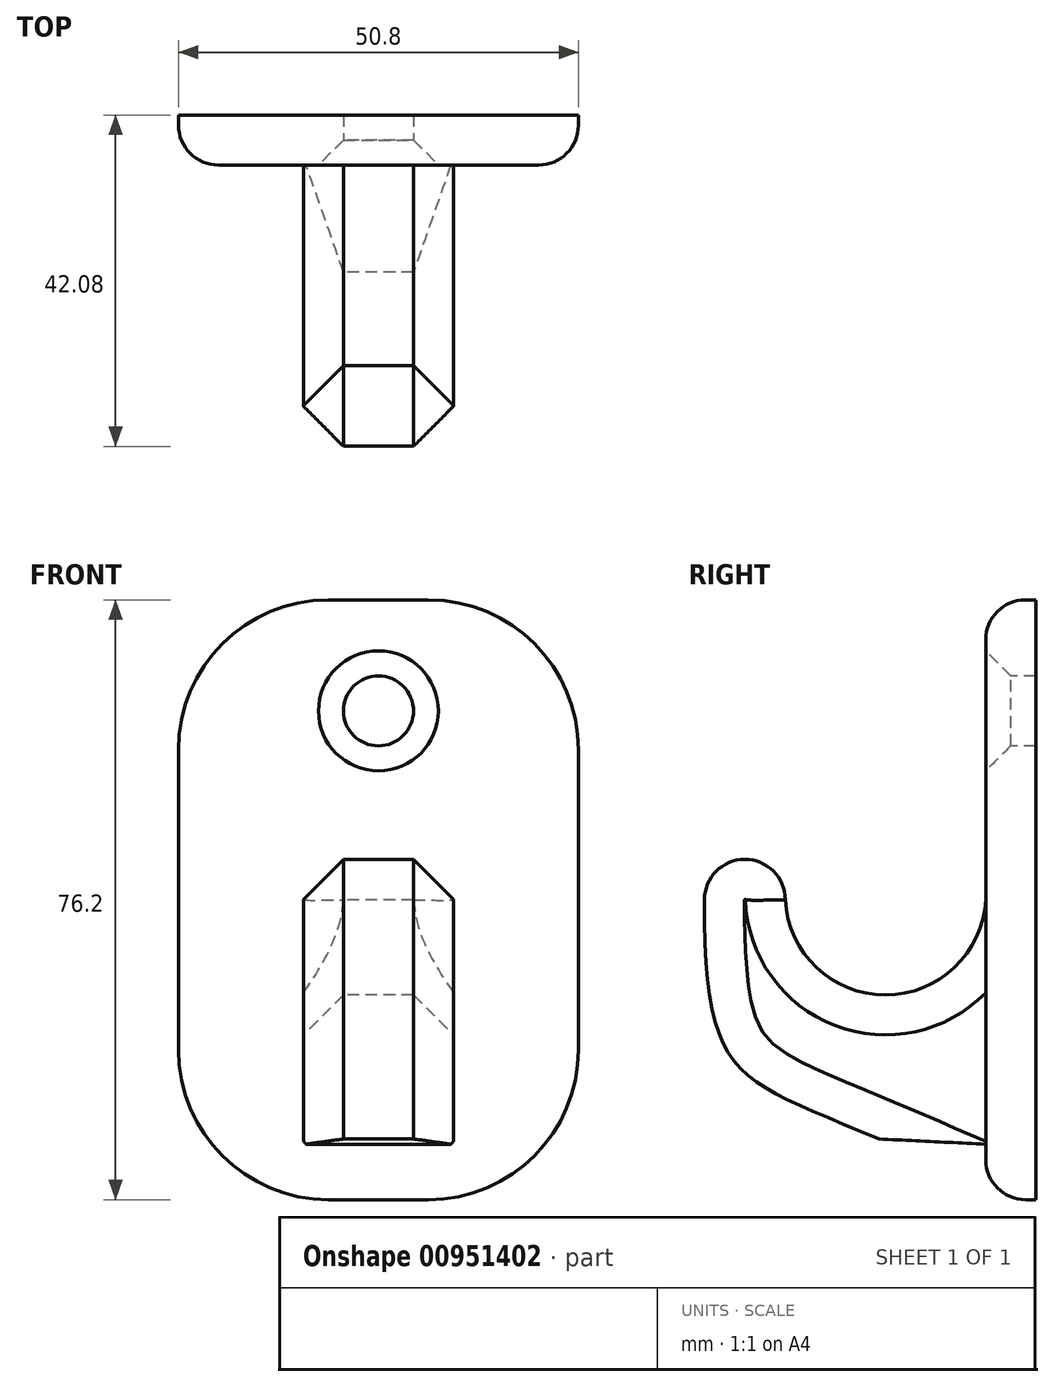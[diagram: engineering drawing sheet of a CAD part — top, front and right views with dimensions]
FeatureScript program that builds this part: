
annotation { "Feature Type Name" : "Feature", "Feature Type Description" : "" }
export const myFeature = defineFeature(function(context is Context, id is Id, definition is map)
    precondition{}
    {
        {
            var Q0;
            Q0=qCreatedBy(makeId("Front.planeOp"),FACE);
            var sketch = newSketch(context, id + "F0", { "sketchPlane" : qUnion([Q0])});
            skLineSegment(sketch, "E0.bottom", {"start": v(-6.35, 38.1) * mm, "end": v(6.35, 38.1) * mm});
            skLineSegment(sketch, "E0.top", {"start": v(-6.35, -38.1) * mm, "end": v(6.35, -38.1) * mm});
            skLineSegment(sketch, "E0.left", {"start": v(-25.4, 19.05) * mm, "end": v(-25.4, -19.05) * mm});
            skLineSegment(sketch, "E0.right", {"start": v(25.4, 19.05) * mm, "end": v(25.4, -19.05) * mm});
            skPoint(sketch, "E0.middle", {"position": v(0, 0) * mm});
            skPoint(sketch, "E1.visualSharp", {"position": v(-25.4, 38.1) * mm});
            skArc(sketch, "E1.filletArc", {"start": v(-6.35, 38.1) * mm, "mid": v(-19.82, 32.52) * mm, "end": v(-25.4, 19.05) * mm});
            skPoint(sketch, "E2.visualSharp", {"position": v(25.4, 38.1) * mm});
            skArc(sketch, "E2.filletArc", {"start": v(25.4, 19.05) * mm, "mid": v(19.82, 32.52) * mm, "end": v(6.35, 38.1) * mm});
            skPoint(sketch, "E3.visualSharp", {"position": v(25.4, -38.1) * mm});
            skArc(sketch, "E3.filletArc", {"start": v(6.35, -38.1) * mm, "mid": v(19.82, -32.52) * mm, "end": v(25.4, -19.05) * mm});
            skPoint(sketch, "E4.visualSharp", {"position": v(-25.4, -38.1) * mm});
            skArc(sketch, "E4.filletArc", {"start": v(-25.4, -19.05) * mm, "mid": v(-19.82, -32.52) * mm, "end": v(-6.35, -38.1) * mm});
            skPoint(sketch, "E5", {"position": v(0, 24) * mm});
            skSolve(sketch);
        }
        {
            var Q0;
            Q0=makeQuery(id+"F0.imprint","IMPRINT",FACE,{"disambiguationData":[TD([[makeQuery(id+"F0.imprint","IMPRINT",EDGE,{"derivedFrom":sQuery(id+"F0.wireOp",EDGE,"E0.bottom")}),-1.0]])]});
            extrude(context, id + "F1", {"entities" : qUnion([Q0]), "oppositeDirection" : true, "depth" : 6.35 * mm, "offsetDistance" : 25.4 * mm});
        }
        {
            var Q0;
            Q0=makeQuery(id+"F1.opExtrude","CAP_EDGE",EDGE,{"disambiguationData":[OSD([sQuery(id+"F0.wireOp",EDGE,"E0.left")])],"isStart":true});
            fillet(context, id + "F2", {"entities" : qUnion([Q0]), "radius" : 5.08 * mm, "tangentPropagation" : true, "allowEdgeOverflow" : false});
        }
        {
            var Q0;
            Q0=sQuery(id+"F0.wireOp",VERTEX,"E5");
            var Q1;
            Q1=makeQuery(id+"F1.opExtrude","SWEPT_BODY",BODY,{"disambiguationData":[OSD([sQuery(id+"F0.wireOp",EDGE,"E0.bottom"),sQuery(id+"F0.wireOp",EDGE,"E0.top"),sQuery(id+"F0.wireOp",EDGE,"E0.left"),sQuery(id+"F0.wireOp",EDGE,"E0.right"),sQuery(id+"F0.wireOp",EDGE,"E1.filletArc"),sQuery(id+"F0.wireOp",EDGE,"E2.filletArc"),sQuery(id+"F0.wireOp",EDGE,"E3.filletArc"),sQuery(id+"F0.wireOp",EDGE,"E4.filletArc")])]});
            hole(context, id + "F3", {"style" : HoleStyle.C_SINK, "endStyle" : HoleEndStyle.THROUGH, "holeDiameter" : 8.9 * mm, "cSinkDiameter" : 15.24 * mm, "cSinkAngle" : 90 * degree, "majorDiameter" : 6.35 * mm, "isTappedThrough" : true, "tappedDepth" : 12.7 * mm, "tapClearance" : 3, "locations" : qUnion([Q0]), "scope" : qUnion([Q1])});
        }
        {
            var Q0;
            Q0=qCreatedBy(makeId("Right.planeOp"),FACE);
            var sketch = newSketch(context, id + "F4", { "sketchPlane" : qUnion([Q0])});
            skArc(sketch, "E6", {"start": v(-25.46, 0) * mm, "mid": v(-12.73, -12.09) * mm, "end": v(0, 0) * mm});
            skLineSegment(sketch, "E7", {"start": v(-13.59, -30.4) * mm, "end": v(0, -31.05) * mm});
            skPoint(sketch, "E8.orphan", {"position": v(0, -18.32) * mm});
            skArc(sketch, "E9", {"start": v(-25.46, 0) * mm, "mid": v(-30.6, 5.13) * mm, "end": v(-35.73, 0) * mm});
            skFitSpline(sketch, "E10", {"points": [v(-35.73, 0) * mm, v(-13.59, -30.4) * mm], "startDerivative": vector(0, -69.6) * mm, "endDerivative": vector(55.2, -23.66) * mm});
            skLineSegment(sketch, "E11", {"start": v(0, 0) * mm, "end": v(0, -31.05) * mm});
            skSolve(sketch);
        }
        {
            var Q0;
            Q0=makeQuery(id+"F4.imprint","IMPRINT",FACE,{"disambiguationData":[TD([[makeQuery(id+"F4.imprint","IMPRINT",EDGE,{"derivedFrom":sQuery(id+"F4.wireOp",EDGE,"E6")}),-1.0]])]});
            extrude(context, id + "F5", {"entities" : qUnion([Q0]), "operationType" : NewBodyOperationType.ADD, "endBound" : BoundingType.SYMMETRIC, "depth" : 19.05 * mm, "offsetDistance" : 25.4 * mm});
        }
        {
            var Q0;
            Q0=makeQuery(id+"F5.opExtrude","CAP_EDGE",EDGE,{"disambiguationData":[OSD([sQuery(id+"F4.wireOp",EDGE,"E6")])],"isStart":false});
            var Q1;
            Q1=makeQuery(id+"F5.opExtrude","CAP_EDGE",EDGE,{"disambiguationData":[OSD([sQuery(id+"F4.wireOp",EDGE,"E6")])],"isStart":true});
            var Q2;
            Q2=makeQuery(id+"F5.opExtrude","CAP_EDGE",EDGE,{"disambiguationData":[OSD([sQuery(id+"F4.wireOp",EDGE,"E10")])],"isStart":false});
            var Q3;
            Q3=makeQuery(id+"F5.opExtrude","CAP_EDGE",EDGE,{"disambiguationData":[OSD([sQuery(id+"F4.wireOp",EDGE,"E10")])],"isStart":true});
            chamfer(context, id + "F6", {"entities" : qUnion([Q0, Q1, Q2, Q3]), "width" : 5.08 * mm, "tangentPropagation" : true});
        }
    });
